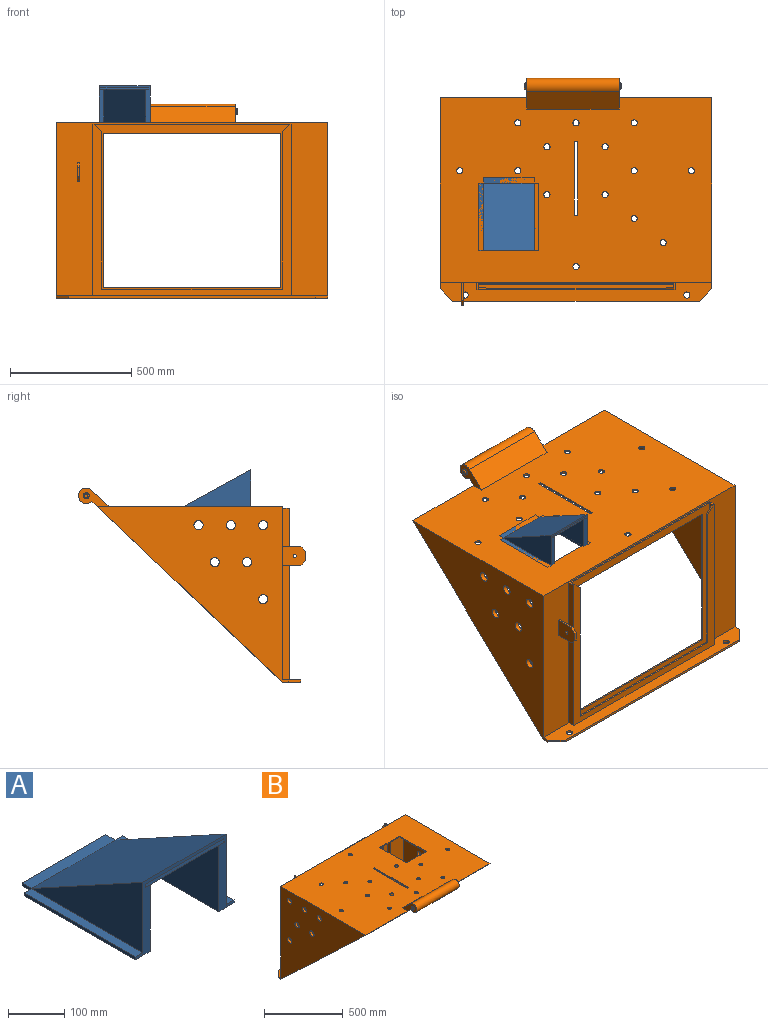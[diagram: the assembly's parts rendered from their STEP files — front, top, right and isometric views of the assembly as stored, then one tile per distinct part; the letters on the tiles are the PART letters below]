
ASSEMBLY  parts=2 mates=1
PART A: 26 faces, bbox 247.7x302.8x164.3 mm
  f0: plane 277.95x152.4mm, normal (1,0,0), area 21180.1mm2, adj f4,f5,f7
  f1: plane 24.15x6.35mm, normal (1,0,0), area 153.4mm2, adj f6,f7,f12,f14
  f2: plane 24.24x6.35mm, normal (-1,0,0), area 153.9mm2, adj f6,f7,f8,f12
  f3: plane 277.95x152.4mm, normal (-1,0,0), area 21180.1mm2, adj f4,f5,f7
  f4: plane 277.95x209.55mm, normal (0,0.48,0.88), area 66425.7mm2, adj f0,f3,f5,f7
  f5: plane 209.55x158.75mm, normal (0,-1,0), area 7106mm2, adj f0,f3,f4,f6,f11,f15,f17,f18
  f6: plane 302.26x247.65mm, normal (0,0,-1), area 26216mm2, adj f1,f2,f5,f8,f9,f10,f11,f12
  f7: plane 302.26x247.65mm, normal (0,0,1), area 15682.5mm2, adj f0,f1,f2,f3,f4,f8,f9,f10
  f8: plane 19.05x6.35mm, normal (0,1,0), area 121mm2, adj f2,f6,f7,f9
  f9: plane 278.03x6.35mm, normal (-1,0,0), area 1765.5mm2, adj f6,f7,f8,f10
  f10: plane 19.05x6.35mm, normal (0,-1,0), area 121mm2, adj f6,f7,f9,f11
  f11: plane 6.35x0.03mm, normal (1,0,0), area 0.2mm2, adj f5,f6,f7,f10
  f12: plane 209.55x6.35mm, normal (0,1,0), area 1330.6mm2, adj f1,f2,f6,f7
  f13: plane 278.11x6.35mm, normal (1,0,0), area 1766mm2, adj f6,f7,f14,f16
  f14: plane 19.05x6.35mm, normal (0,1,0), area 121mm2, adj f1,f6,f7,f13
  f15: plane 6.35x0.03mm, normal (-1,0,0), area 0.2mm2, adj f5,f6,f7,f16
  f16: plane 19.05x6.35mm, normal (0,-1,0), area 121mm2, adj f6,f7,f13,f15
  f17: plane 7.24x0.6mm, normal (-1,0,0), area 2.2mm2, adj f5,f22,f23
  f18: plane 7.24x0.6mm, normal (1,0,0), area 2.2mm2, adj f5,f22,f23
  f19: plane 13.21x5.57mm, normal (-1,0,0), area 36.8mm2, adj f6,f20,f23
  f20: plane 196.85x5.57mm, normal (0,0.88,-0.48), area 1250mm2, adj f6,f19,f21,f23
  f21: plane 13.21x5.57mm, normal (1,0,0), area 36.8mm2, adj f6,f20,f23
  f22: plane 196.85x6.91mm, normal (0,-1,0.09), area 1365.5mm2, adj f5,f17,f18,f23
  f23: plane 273.88x196.85mm, normal (0,-0.48,-0.88), area 53863.2mm2, adj f5,f6,f17,f18,f19,f20,f21,f22
  f24: plane 263.12x144.27mm, normal (1,0,0), area 18979.6mm2, adj f5,f6,f23
  f25: plane 263.12x144.27mm, normal (-1,0,0), area 18979.6mm2, adj f5,f6,f23
PART B: 99 faces, bbox 1117.6x936.6x800.8 mm
  f0: plane 1117.6x762mm, normal (0,0,1), area 779860.9mm2, adj f1,f17,f34,f39,f40,f41,f42,f51
  f1: plane 787.4x723.9mm, normal (-1,0,0), area 269207.3mm2, adj f0,f17,f18,f66,f68,f70,f72,f74
  f2: plane 136.53x0.33mm, normal (0,0,1), area 45.6mm2, adj f31,f35,f37,f88
  f3: plane 819.15x708.06mm, normal (0,1,0), area 74185.4mm2, adj f6,f7,f8,f9,f10,f11,f12,f13
  f4: plane 806.45x708.03mm, normal (0,-1,0), area 65193.4mm2, adj f5,f6,f9,f10,f11,f12,f13,f14
  f5: plane 708.03x15.88mm, normal (1,0,0), area 11239.9mm2, adj f4,f16,f19,f81
  f6: plane 708.06x28.58mm, normal (-1,0,0), area 11241mm2, adj f3,f4,f10,f15,f16,f17,f19,f81
  f7: plane 708.03x28.58mm, normal (1,0,0), area 20231.8mm2, adj f3,f15,f17,f18
  f8: plane 708.03x28.58mm, normal (-1,0,0), area 20231.8mm2, adj f3,f16,f17,f18
  f9: plane 31.71x31.39mm, normal (-0.7,0,0.71), area 283.3mm2, adj f3,f4,f10,f14
  f10: plane 6.35x0.04mm, normal (0,0,1), area 0.2mm2, adj f3,f4,f6,f9
  f11: plane 31.75x31.39mm, normal (0.7,0,0.71), area 283.5mm2, adj f3,f4,f12,f16
  f12: plane 648.06x6.35mm, normal (1,0,0), area 4115.2mm2, adj f3,f4,f11,f13
  f13: plane 742.95x6.35mm, normal (0,0,1), area 4717.7mm2, adj f3,f4,f12,f14
  f14: plane 648.06x6.35mm, normal (-1,0,0), area 4115.2mm2, adj f3,f4,f9,f13
  f15: plane 28.58x6.35mm, normal (0.01,0,1), area 181.5mm2, adj f3,f6,f7,f17
  f16: plane 812.8x28.58mm, normal (0,0,1), area 5302.4mm2, adj f3,f5,f6,f8,f11,f17,f19
  f17: plane 1117.6x714.38mm, normal (0,1,0), area 217680.9mm2, adj f0,f1,f6,f7,f8,f15,f16,f18
  f18: plane 1117.6x76.2mm, normal (0,0,1), area 58159.9mm2, adj f1,f3,f7,f8,f17,f34,f82,f83
  f19: plane 806.45x708.03mm, normal (0,1,0), area 107278mm2, adj f5,f6,f16,f22,f23,f24,f25,f81
  f20: plane 1079.5x748.97mm, normal (0,0,-1), area 739277.7mm2, adj f31,f32,f33,f35,f36,f37,f38,f39
  f21: plane 136.53x0.33mm, normal (0,0,1), area 45.6mm2, adj f32,f36,f38,f88
  f22: plane 635x6.35mm, normal (1,0,0), area 4032.3mm2, adj f19,f23,f25,f26
  f23: plane 730.25x6.35mm, normal (0,0,-1), area 4637.1mm2, adj f19,f22,f24,f26
  f24: plane 635x6.35mm, normal (-1,0,0), area 4032.3mm2, adj f19,f23,f25,f26
  f25: plane 730.25x6.35mm, normal (0,0,1), area 4637.1mm2, adj f19,f22,f24,f26
  f26: plane 793.75x698.5mm, normal (0,-1,0), area 90725.6mm2, adj f22,f23,f24,f25,f27,f28,f29,f30
  f27: plane 793.75x25.4mm, normal (0,0,-1), area 20161.2mm2, adj f26,f28,f30,f33
  f28: plane 698.5x25.4mm, normal (1,0,0), area 17673.1mm2, adj f26,f27,f29,f33,f88
  f29: plane 793.75x13.37mm, normal (0,0,1), area 10611.2mm2, adj f26,f28,f30,f88
  f30: plane 698.5x25.4mm, normal (-1,0,0), area 17673.1mm2, adj f26,f27,f29,f33,f88
  f31: plane 711.2x19.05mm, normal (-1,0,0), area 13382mm2, adj f2,f20,f33,f37,f88
  f32: plane 711.2x19.05mm, normal (1,0,0), area 13382mm2, adj f20,f21,f33,f38,f88
  f33: plane 806.45x693.42mm, normal (0,-1,0), area 13846.7mm2, adj f20,f27,f28,f30,f31,f32,f88
  f34: plane 787.4x723.9mm, normal (1,0,0), area 269207.3mm2, adj f0,f17,f18,f65,f67,f69,f71,f73
  f35: plane 748.97x711.2mm, normal (1,0,0), area 259610.5mm2, adj f2,f20,f37,f66,f68,f70,f72,f74
  f36: plane 748.97x711.2mm, normal (-1,0,0), area 259610.5mm2, adj f20,f21,f38,f65,f67,f69,f71,f73
  f37: plane 711.2x136.53mm, normal (0,-1,0), area 97096.6mm2, adj f2,f20,f31,f35
  f38: plane 711.2x136.53mm, normal (0,-1,0), area 97096.6mm2, adj f20,f21,f32,f36
  f39: plane 241.3x6.35mm, normal (1,0,0), area 1532.3mm2, adj f0,f20,f40,f42
  f40: plane 177.8x6.35mm, normal (0,1,0), area 1129mm2, adj f0,f20,f39,f41
  f41: plane 241.3x6.35mm, normal (-1,0,0), area 1532.3mm2, adj f0,f20,f40,f42
  f42: plane 177.8x6.35mm, normal (0,-1,0), area 1129mm2, adj f0,f20,f39,f41
  f43: plane 76.2x9.53mm, normal (0,0,-1), area 725.8mm2, adj f17,f44,f46,f49
  f44: plane 95.25x76.2mm, normal (1,0,0), area 6768.5mm2, adj f17,f43,f45,f47,f48,f49,f50
  f45: plane 76.2x9.53mm, normal (0,0,1), area 725.8mm2, adj f17,f44,f46,f48
  f46: plane 95.25x76.2mm, normal (-1,0,0), area 6768.5mm2, adj f17,f43,f45,f47,f48,f49,f50
  f47: plane 38.1x9.53mm, normal (0,1,0), area 362.9mm2, adj f44,f46,f48,f49
  f48: plane 19.05x19.05mm, normal (0,0.71,0.71), area 256.6mm2, adj f44,f45,f46,f47
  f49: plane 19.05x19.05mm, normal (0,0.71,-0.71), area 256.6mm2, adj f43,f44,f46,f47
  f50: cylinder r=6.35mm len=12.7mm, axis (-1,0,0), area 380mm2, adj f44,f46
  f51: cylinder r=12.7mm len=25.4mm, axis (0,0,1), area 506.7mm2, adj f0,f20
  f52: cylinder r=12.7mm len=25.4mm, axis (0,0,1), area 506.7mm2, adj f0,f20
  f53: cylinder r=12.7mm len=25.4mm, axis (0,0,1), area 506.7mm2, adj f0,f20
  f54: cylinder r=12.7mm len=25.4mm, axis (0,0,1), area 506.7mm2, adj f0,f20
  f55: cylinder r=12.7mm len=25.4mm, axis (0,0,1), area 506.7mm2, adj f0,f20
  f56: cylinder r=12.7mm len=25.4mm, axis (0,0,1), area 506.7mm2, adj f0,f20
  f57: cylinder r=12.7mm len=25.4mm, axis (0,0,1), area 506.7mm2, adj f0,f20
  f58: cylinder r=12.7mm len=25.4mm, axis (0,0,1), area 506.7mm2, adj f0,f20
  f59: cylinder r=12.7mm len=25.4mm, axis (0,0,1), area 506.7mm2, adj f0,f20
  f60: cylinder r=12.7mm len=25.4mm, axis (0,0,1), area 506.7mm2, adj f0,f20
  f61: cylinder r=12.7mm len=25.4mm, axis (0,0,1), area 506.7mm2, adj f0,f20
  f62: cylinder r=12.7mm len=25.4mm, axis (0,0,1), area 506.7mm2, adj f0,f20
  f63: cylinder r=12.7mm len=25.4mm, axis (0,0,1), area 506.7mm2, adj f0,f20
  f64: cylinder r=12.7mm len=25.4mm, axis (0,0,1), area 506.7mm2, adj f0,f20
  f65: cylinder r=19.05mm len=38.1mm, axis (-1,0,0), area 2280.2mm2, adj f34,f36
  f66: cylinder r=19.05mm len=38.1mm, axis (-1,0,0), area 2280.2mm2, adj f1,f35
  f67: cylinder r=19.05mm len=38.1mm, axis (-1,0,0), area 2280.2mm2, adj f34,f36
  f68: cylinder r=19.05mm len=38.1mm, axis (-1,0,0), area 2280.2mm2, adj f1,f35
  f69: cylinder r=19.05mm len=38.1mm, axis (-1,0,0), area 2280.2mm2, adj f34,f36
  f70: cylinder r=19.05mm len=38.1mm, axis (-1,0,0), area 2280.2mm2, adj f1,f35
  f71: cylinder r=19.05mm len=38.1mm, axis (-1,0,0), area 2280.2mm2, adj f34,f36
  f72: cylinder r=19.05mm len=38.1mm, axis (-1,0,0), area 2280.2mm2, adj f1,f35
  f73: cylinder r=19.05mm len=38.1mm, axis (-1,0,0), area 2280.2mm2, adj f34,f36
  f74: cylinder r=19.05mm len=38.1mm, axis (-1,0,0), area 2280.2mm2, adj f1,f35
  f75: cylinder r=19.05mm len=38.1mm, axis (-1,0,0), area 2280.2mm2, adj f34,f36
  f76: cylinder r=19.05mm len=38.1mm, axis (-1,0,0), area 2280.2mm2, adj f1,f35
  f77: plane 304.8x6.35mm, normal (-1,0,0), area 1935.5mm2, adj f0,f20,f78,f80
  f78: plane 12.7x6.35mm, normal (0,-1,0), area 80.6mm2, adj f0,f20,f77,f79
  f79: plane 304.8x6.35mm, normal (1,0,0), area 1935.5mm2, adj f0,f20,f78,f80
  f80: plane 12.7x6.35mm, normal (0,1,0), area 80.6mm2, adj f0,f20,f77,f79
  f81: plane 806.45x15.88mm, normal (0,0,1), area 12802.4mm2, adj f4,f5,f6,f19
  f82: plane 1016x9.53mm, normal (0,1,0), area 9677.4mm2, adj f18,f83,f84,f87
  f83: plane 50.8x50.8mm, normal (0.71,0.71,0), area 684.3mm2, adj f18,f34,f82,f87
  f84: plane 50.8x50.8mm, normal (-0.71,0.71,0), area 684.3mm2, adj f1,f18,f82,f87
  f85: cylinder r=12.7mm len=25.4mm, axis (0,0,1), area 760.1mm2, adj f18,f87
  f86: cylinder r=12.7mm len=25.4mm, axis (0,0,1), area 760.1mm2, adj f18,f87
  f87: plane 1117.6x76.2mm, normal (0,0,-1), area 81567.1mm2, adj f1,f34,f82,f83,f84,f85,f86,f88
  f88: plane 1117.6x786.56mm, normal (0,-0.69,-0.72), area 80500mm2, adj f0,f1,f2,f20,f21,f28,f29,f30
  f89: cylinder r=31.75mm len=381mm, axis (-1,0,0), area 56934.7mm2, adj f88,f90,f91,f92
  f90: plane 381x72.78mm, normal (0,0.68,0.73), area 38036.5mm2, adj f0,f89,f91,f92
  f91: plane 126.26x76.95mm, normal (1,0,0), area 4511.1mm2, adj f0,f88,f89,f90,f95
  f92: plane 126.26x76.95mm, normal (-1,0,0), area 4511.1mm2, adj f0,f88,f89,f90,f93
  f93: cylinder r=12.7mm len=25.4mm, axis (1,0,0), area 405.4mm2, adj f92,f98
  f94: plane 15.24x15.24mm, normal (-1,0,0), area 182.4mm2, adj f98
  f95: cylinder r=12.7mm len=25.4mm, axis (-1,0,0), area 405.4mm2, adj f91,f97
  f96: plane 15.24x15.24mm, normal (1,0,0), area 182.4mm2, adj f97
  f97: torus R=7.62mm, axis (-1,0,0), area 544.2mm2, adj f95,f96
  f98: torus R=7.62mm, axis (-1,0,0), area 544.2mm2, adj f93,f94
PLACE A t=(928.59,-2503.34,984.31)mm
PLACE B rot(axis=(0,0,-1),180deg) t=(1310.47,-2924.56,628.71)mm
MATE fastened A.f6 <-> B.f20  axis (0,0,-1) through (1033.37,-2516.55,984.31)mm
